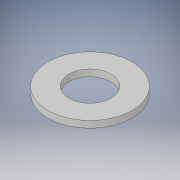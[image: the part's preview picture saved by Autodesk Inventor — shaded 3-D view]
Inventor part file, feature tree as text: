
AUTODESK INVENTOR PART (.ipt)
format: ipt  version: 2017 (Build 210142000, 142)  size: 98,816 bytes
history: native  units: in
note: dims shown in document units (in); Inventor stores cm internally (conversion verified against a paired STEP export)
features: extrude x1, hole x1, sketch x1
ambient origin geometry x8: Origin, YZ Plane, XZ Plane, XY Plane, X Axis, Y Axis, Z Axis, Center Point
bodies: Solid1 (feature_tree)
feature tree (3):
  extrude  "Extrusion1"  Depth=0.01in TaperAngle=0.0deg
  hole  "Hole1"  [1 undecoded]
  sketch  "Sketch1"  dims[d0=0.125in d1=0.01in d2=0.0in d3=1.0in d4=1.0in d5=0.0625in d6=0.75in d7=0.375in d8=0.25in d9=0.5635in d10=0.0625in d11=0.8108in]
note: 1 required parameter value undecoded (feature->parameter linkage not recoverable at this tier; creation-order binding heuristic only, values carry confidence <= 0.55)
